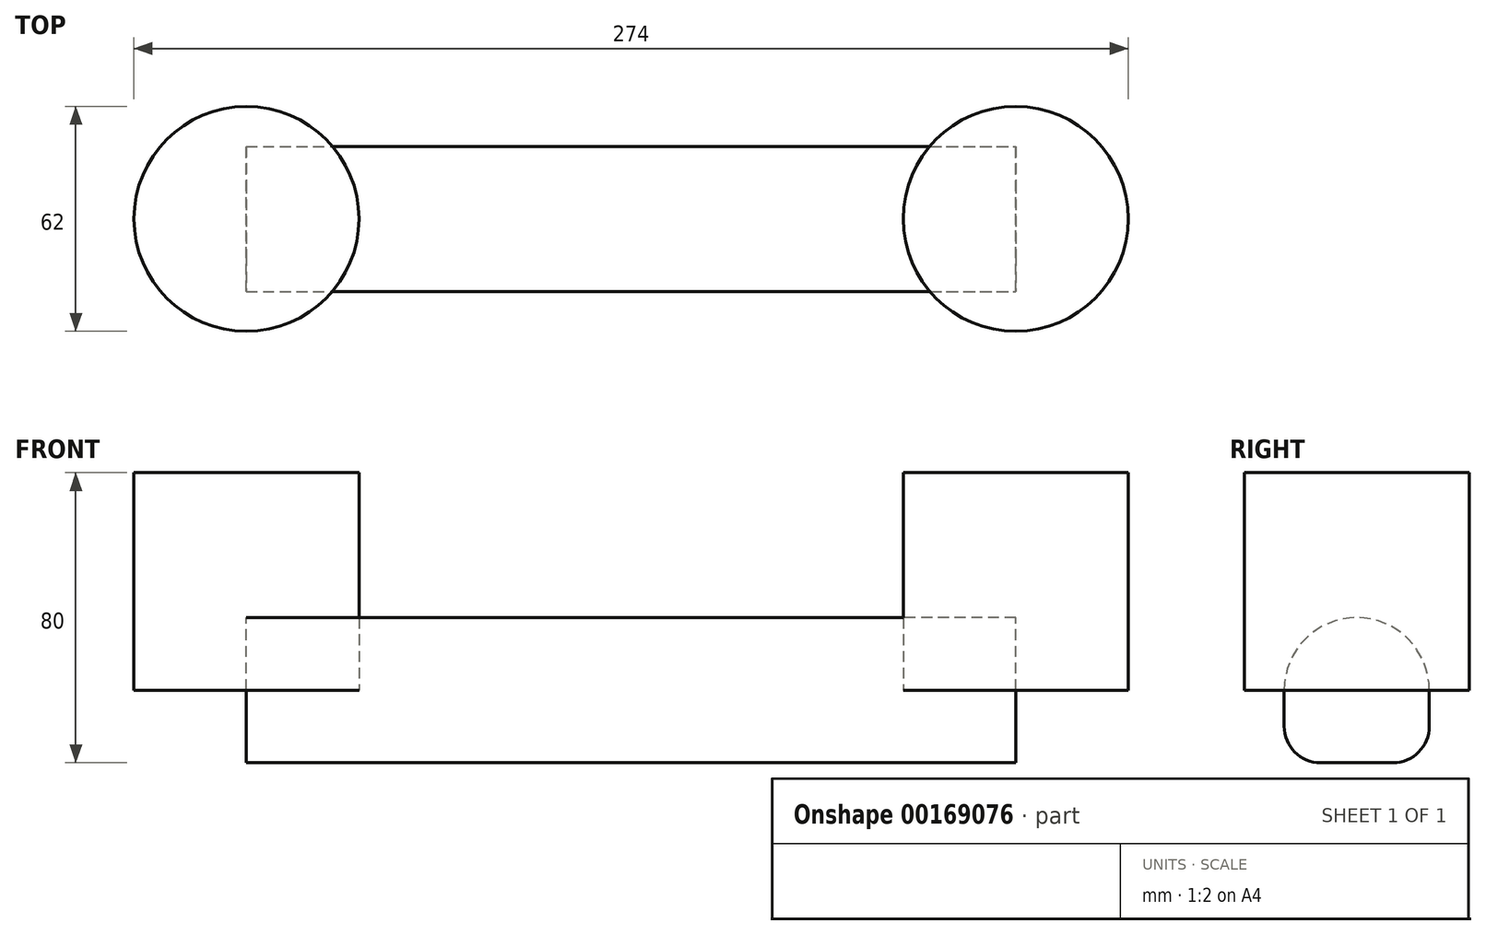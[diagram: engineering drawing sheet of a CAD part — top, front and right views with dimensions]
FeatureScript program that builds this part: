
annotation { "Feature Type Name" : "Feature", "Feature Type Description" : "" }
export const myFeature = defineFeature(function(context is Context, id is Id, definition is map)
    precondition{}
    {
        {
            var Q0;
            Q0=qCreatedBy(makeId("Top.planeOp"),FACE);
            var sketch = newSketch(context, id + "F0", { "sketchPlane" : qUnion([Q0])});
            skCircle(sketch, "E0", {"center": v(-106, 0) * mm, "radius": 31 * mm});
            skCircle(sketch, "E1", {"center": v(106, 0) * mm, "radius": 31 * mm});
            skSolve(sketch);
        }
        {
            var Q0;
            Q0 = qSketchRegion(id + "F0", true);
            extrude(context, id + "F1", {"entities" : qUnion([Q0]), "depth" : 60 * mm});
        }
        {
            var Q0;
            Q0=qCreatedBy(makeId("Top.planeOp"),FACE);
            var sketch = newSketch(context, id + "F2", { "sketchPlane" : qUnion([Q0])});
            skLineSegment(sketch, "E2.bottom", {"start": v(-106, 20) * mm, "end": v(106, 20) * mm});
            skLineSegment(sketch, "E2.top", {"start": v(-106, -20) * mm, "end": v(106, -20) * mm});
            skLineSegment(sketch, "E2.left", {"start": v(-106, 20) * mm, "end": v(-106, -20) * mm});
            skLineSegment(sketch, "E2.right", {"start": v(106, 20) * mm, "end": v(106, -20) * mm});
            skPoint(sketch, "E2.middle", {"position": v(0, 0) * mm});
            skSolve(sketch);
        }
        {
            var Q0;
            Q0 = qSketchRegion(id + "F2", true);
            extrude(context, id + "F3", {"entities" : qUnion([Q0]), "endBound" : BoundingType.SYMMETRIC, "oppositeDirection" : true, "depth" : 40 * mm});
        }
        {
            var Q0;
            Q0=makeQuery(id+"F3.opExtrude","CAP_EDGE",EDGE,{"disambiguationData":[OSD([sQuery(id+"F2.wireOp",EDGE,"E2.bottom")])],"isStart":false});
            var Q1;
            Q1=makeQuery(id+"F3.opExtrude","CAP_EDGE",EDGE,{"disambiguationData":[OSD([sQuery(id+"F2.wireOp",EDGE,"E2.top")])],"isStart":false});
            fillet(context, id + "F4", {"entities" : qUnion([Q0, Q1]), "radius" : 10 * mm, "tangentPropagation" : true, "allowEdgeOverflow" : false});
        }
        {
            var Q0;
            Q0=makeQuery(id+"F3.opExtrude","CAP_EDGE",EDGE,{"disambiguationData":[OSD([sQuery(id+"F2.wireOp",EDGE,"E2.bottom")])],"isStart":true});
            var Q1;
            Q1=makeQuery(id+"F3.opExtrude","CAP_EDGE",EDGE,{"disambiguationData":[OSD([sQuery(id+"F2.wireOp",EDGE,"E2.top")])],"isStart":true});
            fillet(context, id + "F5", {"entities" : qUnion([Q0, Q1]), "radius" : 20 * mm, "tangentPropagation" : true, "allowEdgeOverflow" : false});
        }
    });
